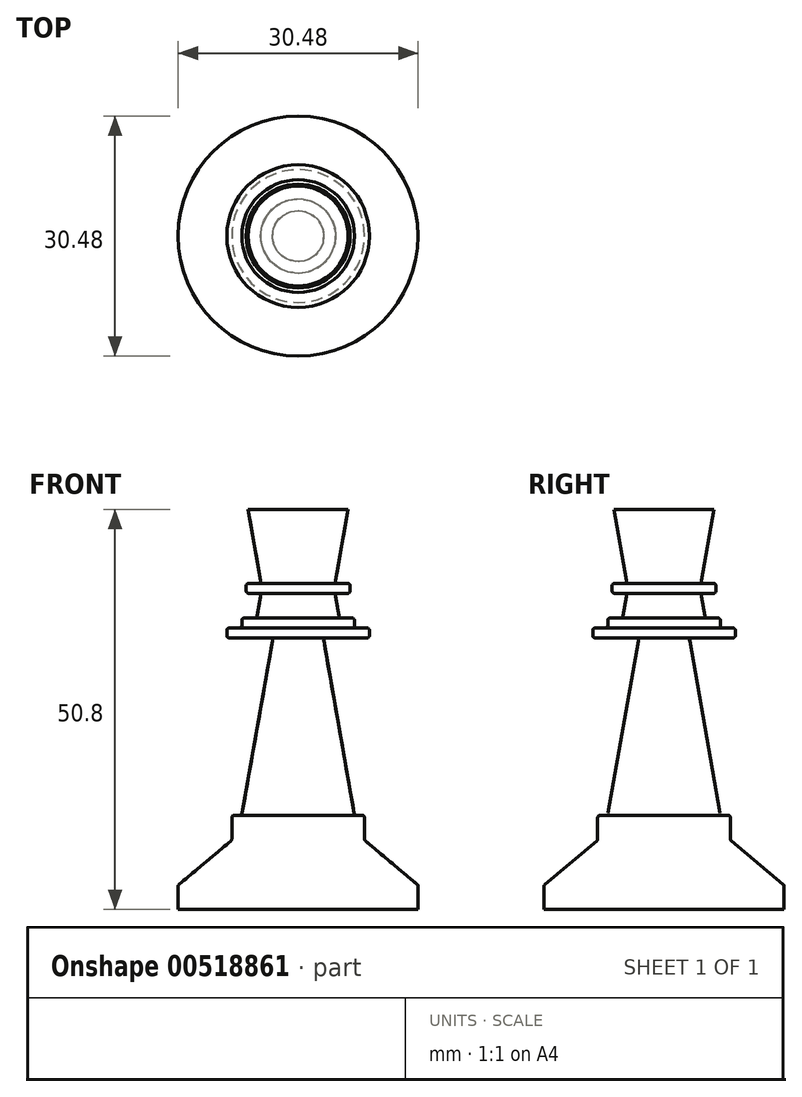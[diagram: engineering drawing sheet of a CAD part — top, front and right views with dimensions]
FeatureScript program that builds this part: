
annotation { "Feature Type Name" : "Feature", "Feature Type Description" : "" }
export const myFeature = defineFeature(function(context is Context, id is Id, definition is map)
    precondition{}
    {
        {
            var Q0;
            Q0=qCreatedBy(makeId("Front.planeOp"),FACE);
            var sketch = newSketch(context, id + "F0", { "sketchPlane" : qUnion([Q0])});
            skLineSegment(sketch, "E0.bottom", {"start": v(0, 0) * mm, "end": v(-15.24, 0) * mm});
            skLineSegment(sketch, "E0.top", {"start": v(0, 50.8) * mm, "end": v(-6.35, 50.8) * mm});
            skLineSegment(sketch, "E0.left", {"start": v(0, 0) * mm, "end": v(0, 50.8) * mm});
            skLineSegment(sketch, "E1", {"start": v(-15.24, 0) * mm, "end": v(-15.24, 2.93) * mm});
            skLineSegment(sketch, "E2", {"start": v(-15.13, 3.18) * mm, "end": v(-8.54, 8.7) * mm});
            skLineSegment(sketch, "E3", {"start": v(-8.43, 8.94) * mm, "end": v(-8.43, 11.65) * mm});
            skLineSegment(sketch, "E4", {"start": v(-8.11, 11.97) * mm, "end": v(-7.43, 11.97) * mm});
            skLineSegment(sketch, "E5", {"start": v(-7.11, 12.23) * mm, "end": v(-3.26, 34.11) * mm});
            skLineSegment(sketch, "E6", {"start": v(-3.57, 34.48) * mm, "end": v(-8.74, 34.48) * mm});
            skLineSegment(sketch, "E7", {"start": v(-9.06, 34.8) * mm, "end": v(-9.06, 35.44) * mm});
            skLineSegment(sketch, "E8", {"start": v(-8.74, 35.75) * mm, "end": v(-7.47, 35.75) * mm});
            skLineSegment(sketch, "E9", {"start": v(-7.15, 36.07) * mm, "end": v(-7.15, 36.7) * mm});
            skLineSegment(sketch, "E10", {"start": v(-6.83, 37.02) * mm, "end": v(-5.51, 37.02) * mm});
            skLineSegment(sketch, "E11", {"start": v(-5.2, 37.29) * mm, "end": v(-4.76, 39.78) * mm});
            skLineSegment(sketch, "E12", {"start": v(-5.07, 40.15) * mm, "end": v(-6.28, 40.15) * mm});
            skLineSegment(sketch, "E13", {"start": v(-6.6, 40.47) * mm, "end": v(-6.6, 41.1) * mm});
            skLineSegment(sketch, "E14", {"start": v(-6.28, 41.42) * mm, "end": v(-5.07, 41.42) * mm});
            skLineSegment(sketch, "E15", {"start": v(-4.76, 41.8) * mm, "end": v(-6.35, 50.8) * mm});
            skPoint(sketch, "E16.visualSharp", {"position": v(-15.24, 3.08) * mm});
            skArc(sketch, "E16.filletArc", {"start": v(-15.13, 3.18) * mm, "mid": v(-15.21, 3.07) * mm, "end": v(-15.24, 2.93) * mm});
            skPoint(sketch, "E17.visualSharp", {"position": v(-8.43, 8.8) * mm});
            skArc(sketch, "E17.filletArc", {"start": v(-8.54, 8.7) * mm, "mid": v(-8.46, 8.8) * mm, "end": v(-8.43, 8.94) * mm});
            skPoint(sketch, "E18.visualSharp", {"position": v(-3.2, 34.48) * mm});
            skArc(sketch, "E18.filletArc", {"start": v(-3.26, 34.11) * mm, "mid": v(-3.33, 34.37) * mm, "end": v(-3.57, 34.48) * mm});
            skPoint(sketch, "E19.visualSharp", {"position": v(-8.43, 11.97) * mm});
            skArc(sketch, "E19.filletArc", {"start": v(-8.11, 11.97) * mm, "mid": v(-8.34, 11.88) * mm, "end": v(-8.43, 11.65) * mm});
            skPoint(sketch, "E20.visualSharp", {"position": v(-7.16, 11.97) * mm});
            skArc(sketch, "E20.filletArc", {"start": v(-7.43, 11.97) * mm, "mid": v(-7.22, 12.04) * mm, "end": v(-7.11, 12.23) * mm});
            skPoint(sketch, "E21.visualSharp", {"position": v(-9.06, 34.48) * mm});
            skArc(sketch, "E21.filletArc", {"start": v(-9.06, 34.8) * mm, "mid": v(-8.96, 34.58) * mm, "end": v(-8.74, 34.48) * mm});
            skPoint(sketch, "E22.visualSharp", {"position": v(-9.06, 35.75) * mm});
            skArc(sketch, "E22.filletArc", {"start": v(-8.74, 35.75) * mm, "mid": v(-8.96, 35.66) * mm, "end": v(-9.06, 35.44) * mm});
            skPoint(sketch, "E23.visualSharp", {"position": v(-7.15, 35.75) * mm});
            skArc(sketch, "E23.filletArc", {"start": v(-7.47, 35.75) * mm, "mid": v(-7.25, 35.85) * mm, "end": v(-7.15, 36.07) * mm});
            skPoint(sketch, "E24.visualSharp", {"position": v(-7.15, 37.02) * mm});
            skArc(sketch, "E24.filletArc", {"start": v(-6.83, 37.02) * mm, "mid": v(-7.06, 36.93) * mm, "end": v(-7.15, 36.7) * mm});
            skPoint(sketch, "E25.visualSharp", {"position": v(-5.25, 37.02) * mm});
            skArc(sketch, "E25.filletArc", {"start": v(-5.51, 37.02) * mm, "mid": v(-5.3, 37.1) * mm, "end": v(-5.2, 37.29) * mm});
            skPoint(sketch, "E26.visualSharp", {"position": v(-4.7, 40.15) * mm});
            skArc(sketch, "E26.filletArc", {"start": v(-4.76, 39.78) * mm, "mid": v(-4.83, 40.04) * mm, "end": v(-5.07, 40.15) * mm});
            skPoint(sketch, "E27.visualSharp", {"position": v(-6.6, 40.15) * mm});
            skArc(sketch, "E27.filletArc", {"start": v(-6.6, 40.47) * mm, "mid": v(-6.5, 40.24) * mm, "end": v(-6.28, 40.15) * mm});
            skPoint(sketch, "E28.visualSharp", {"position": v(-6.6, 41.42) * mm});
            skArc(sketch, "E28.filletArc", {"start": v(-6.28, 41.42) * mm, "mid": v(-6.5, 41.33) * mm, "end": v(-6.6, 41.1) * mm});
            skPoint(sketch, "E29.visualSharp", {"position": v(-4.7, 41.42) * mm});
            skArc(sketch, "E29.filletArc", {"start": v(-5.07, 41.42) * mm, "mid": v(-4.83, 41.53) * mm, "end": v(-4.76, 41.8) * mm});
            skSolve(sketch);
        }
        {
            var Q0;
            Q0=makeQuery(id+"F0.imprint","IMPRINT",FACE,{"disambiguationData":[TD([[makeQuery(id+"F0.imprint","IMPRINT",EDGE,{"derivedFrom":sQuery(id+"F0.wireOp",EDGE,"E0.bottom")}),-1.0]])]});
            var Q1;
            Q1=sQuery(id+"F0.wireOp",EDGE,"E0.left");
            revolve(context, id + "F1", {"entities" : qUnion([Q0]), "axis" : qUnion([Q1]), "revolveType" : RevolveType.FULL, "oppositeDirection" : true});
        }
        {
            var Q0;
            Q0=makeQuery(id+"F0.imprint","IMPRINT",FACE,{"disambiguationData":[TD([[makeQuery(id+"F0.imprint","IMPRINT",EDGE,{"derivedFrom":sQuery(id+"F0.wireOp",EDGE,"E0.bottom")}),-1.0]])]});
            var Q1;
            Q1=sQuery(id+"F0.wireOp",EDGE,"E0.left");
            revolve(context, id + "F2", {"entities" : qUnion([Q0]), "axis" : qUnion([Q1]), "revolveType" : RevolveType.FULL});
        }
    });
